# Revit family: Liv_In-Wall_Water Dispenser-Elkay-LBWD00WHC_BKC
name_source: partatom
category: Plumbing Fixtures
units: mm (PartAtom-declared; Revit-internal decimal feet)

## family parameters
Cut with Voids When Loaded = No
Host = Face
Maintain Annotation Orientation = No
OmniClass Number = 23.65.70.14.11
OmniClass Title = Drinking Fountains/Coolers
Part Type = Normal
Room Calculation Point = No
Round Connector Dimension = Use Diameter
Shared = No

## types (2) — shared parameters
Activation Method = Electronic Bottle Filler Sensor
Approx. Shipping Weight (lbs) = 40
Assembly Code = D2010
CW Connection = No
Current = 0 A
Default Elevation = 48 "
Height = 28 "
Inlet connection = 0.38 "
Length = 5.13 "
Main Material = Finish-Elkay-Stainless Steel
Manufacturer = Elkay Manufacturer Company
Manufacturer Brand = Elkay (by Zurn Elkay Water Solutions)
Number of Poles = 1
Outlet connection = 1.25 "
Product Documentation Link = https://www.elkayfiles.com
Product Installation Sheet URL = https://www.elkayfiles.com
Product Page URL = https://www.elkay.com
Product Weight (lbs) = 25
Product data URL = https://bimobject.com
Repair Parts URL = https://www.elkayfiles.com
Second material = Elkay-Transparent
URL = https://www.elkay.com
Voltage = 115 V
Waste Connection = No
Width = 18 "
zero-valued in all types: Power Factor

## per-type parameters (varying)
| type | Description | Material_Front Panel | Model |
| LBWD00WHC ( Filtered Water Dispenser Non refrigerated Aspen White) | Liv®In-Wall Commercial Filtered Water Dispenser Non-refrigerated Aspen White | Finish-Elkay-Aspen White | LBWD00WHC |
| LBWD00BKC (Filtered Water Dispenser Non refrigerated Midnight) | Liv®  In-Wall Filtered Water Dispenser Non-refrigerated Midnight | Finish-Elkay-Midnight Black | LBWD00BKC |

## geometry (parser evidence)
native form markers: Sweep x5
no freeform markers — native parametric forms only
